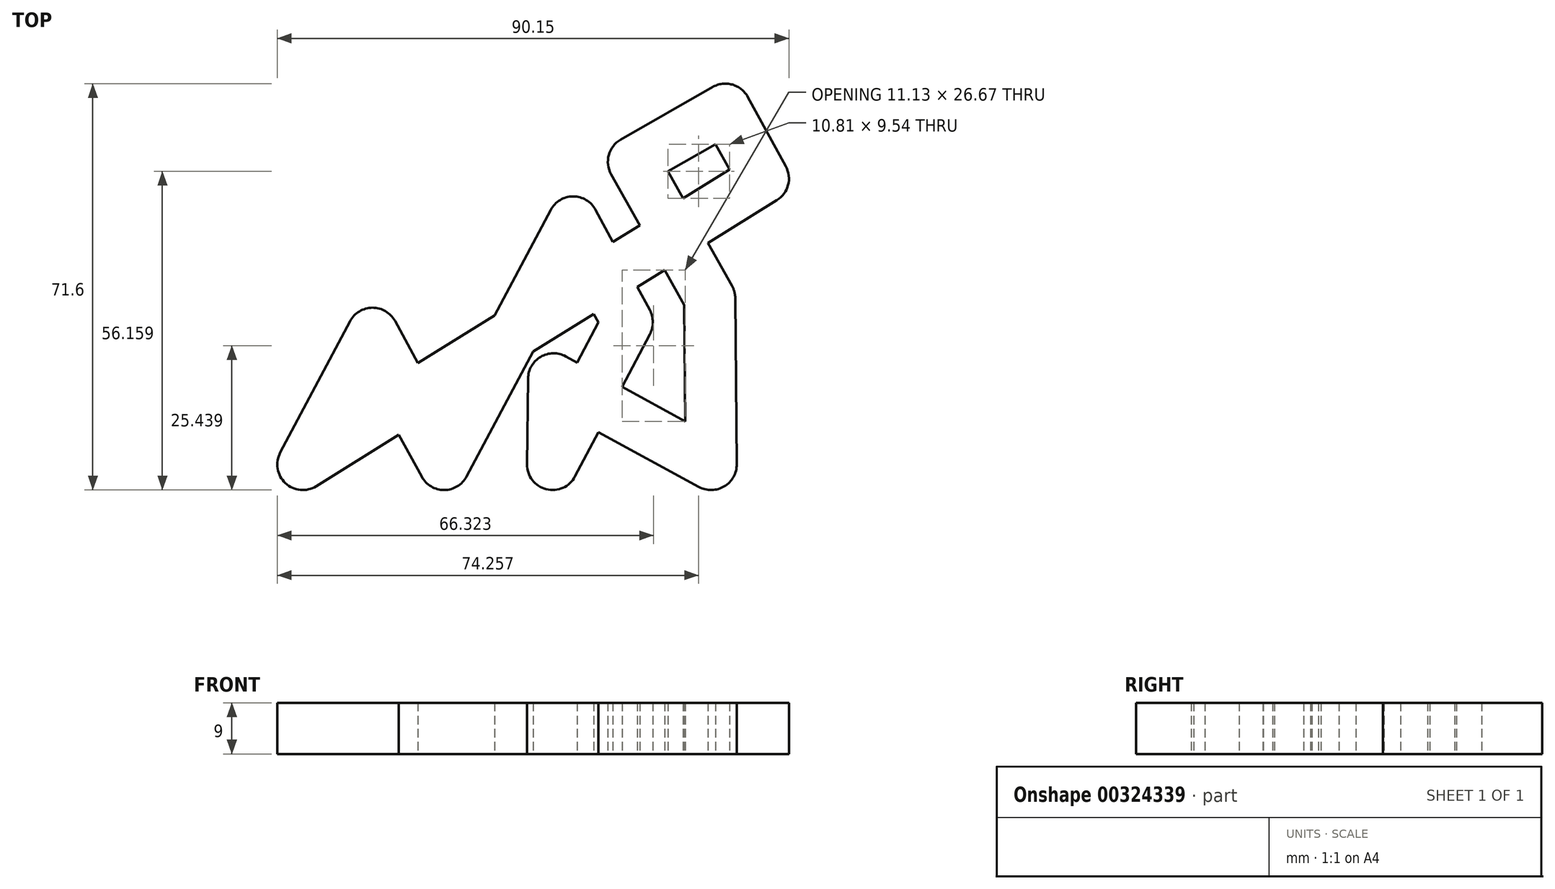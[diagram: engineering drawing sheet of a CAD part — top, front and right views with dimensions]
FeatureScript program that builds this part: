
annotation { "Feature Type Name" : "Feature", "Feature Type Description" : "" }
export const myFeature = defineFeature(function(context is Context, id is Id, definition is map)
    precondition{}
    {
        {
            var Q0;
            Q0=qCreatedBy(makeId("Top.planeOp"),FACE);
            var sketch = newSketch(context, id + "F0", { "sketchPlane" : qUnion([Q0])});
            skCircle(sketch, "E0", {"center": v(-54.94, 12.42) * mm, "radius": 4.5 * mm});
            skCircle(sketch, "E1", {"center": v(-67.23, -10.7) * mm, "radius": 4.5 * mm});
            skCircle(sketch, "E2", {"center": v(-42.34, -10.7) * mm, "radius": 4.5 * mm});
            skCircle(sketch, "E3", {"center": v(-23.23, -10.7) * mm, "radius": 4.5 * mm});
            skCircle(sketch, "E4", {"center": v(4.72, -10.7) * mm, "radius": 4.5 * mm});
            skCircle(sketch, "E5", {"center": v(-19.6, 32.03) * mm, "radius": 4.5 * mm});
            skCircle(sketch, "E6", {"center": v(13.92, 39.66) * mm, "radius": 4.5 * mm});
            skCircle(sketch, "E7", {"center": v(7.22, 51.9) * mm, "radius": 4.5 * mm});
            skCircle(sketch, "E8", {"center": v(-8.98, 42.62) * mm, "radius": 4.5 * mm});
            skCircle(sketch, "E9", {"center": v(4.47, 18.56) * mm, "radius": 4.5 * mm});
            skCircle(sketch, "E10", {"center": v(-10.06, 14.34) * mm, "radius": 4.5 * mm});
            skLineSegment(sketch, "E11", {"start": v(-58.92, 14.53) * mm, "end": v(-71.2, -8.6) * mm});
            skLineSegment(sketch, "E12", {"start": v(-63.26, -12.82) * mm, "end": v(-50.97, 10.3) * mm});
            skLineSegment(sketch, "E13", {"start": v(-51, 14.57) * mm, "end": v(-38.4, -8.56) * mm});
            skLineSegment(sketch, "E14", {"start": v(-58.9, 10.26) * mm, "end": v(-46.3, -12.86) * mm});
            skLineSegment(sketch, "E15", {"start": v(-69.6, -6.88) * mm, "end": v(11.55, 43.48) * mm});
            skCircle(sketch, "E16", {"center": v(-23.04, 4.38) * mm, "radius": 4.5 * mm});
            skLineSegment(sketch, "E17", {"start": v(-64.86, -14.53) * mm, "end": v(16.3, 35.84) * mm});
            skLineSegment(sketch, "E18", {"start": v(-38.37, -12.82) * mm, "end": v(-15.62, 29.91) * mm});
            skLineSegment(sketch, "E19", {"start": v(-46.32, -8.6) * mm, "end": v(-23.56, 34.14) * mm});
            skLineSegment(sketch, "E20", {"start": v(-23.55, 29.9) * mm, "end": v(-14.02, 12.2) * mm});
            skLineSegment(sketch, "E21", {"start": v(-15.63, 34.16) * mm, "end": v(-6.1, 16.47) * mm});
            skLineSegment(sketch, "E22", {"start": v(-6.08, 12.24) * mm, "end": v(-19.25, -12.8) * mm});
            skLineSegment(sketch, "E23", {"start": v(-14.04, 16.43) * mm, "end": v(-27.22, -8.61) * mm});
            skLineSegment(sketch, "E24", {"start": v(-27.73, -10.65) * mm, "end": v(-27.54, 4.44) * mm});
            skLineSegment(sketch, "E25", {"start": v(-18.73, -10.77) * mm, "end": v(-18.54, 4.32) * mm});
            skLineSegment(sketch, "E26", {"start": v(-25.19, 0.43) * mm, "end": v(2.57, -14.66) * mm});
            skLineSegment(sketch, "E27", {"start": v(-20.9, 8.33) * mm, "end": v(6.87, -6.75) * mm});
            skLineSegment(sketch, "E28", {"start": v(0.22, -10.75) * mm, "end": v(-0.03, 18.52) * mm});
            skLineSegment(sketch, "E29", {"start": v(9.22, -10.67) * mm, "end": v(8.97, 18.6) * mm});
            skLineSegment(sketch, "E30", {"start": v(8.4, 20.76) * mm, "end": v(-5.05, 44.81) * mm});
            skLineSegment(sketch, "E31", {"start": v(0.54, 16.37) * mm, "end": v(-12.9, 40.42) * mm});
            skLineSegment(sketch, "E32", {"start": v(-6.74, 38.71) * mm, "end": v(9.46, 48) * mm});
            skLineSegment(sketch, "E33", {"start": v(-11.21, 46.52) * mm, "end": v(4.99, 55.8) * mm});
            skLineSegment(sketch, "E34", {"start": v(3.28, 49.74) * mm, "end": v(9.97, 37.5) * mm});
            skLineSegment(sketch, "E35", {"start": v(11.16, 54.06) * mm, "end": v(17.87, 41.82) * mm});
            skSolve(sketch);
        }
        {
            var Q0;
            {var subQ0=sQuery(id+"F0.wireOp",EDGE,"E1");var subQ1=makeQuery(id+"F0.imprint","INTERSECT",VERTEX,{"derivedFrom":[subQ0,sQuery(id+"F0.wireOp",EDGE,"E11")]});Q0=makeQuery(id+"F0.imprint","IMPRINT",FACE,{"disambiguationData":[TD([[makeQuery(id+"F0.imprint","IMPRINT",EDGE,{"disambiguationData":[TD([[subQ1,1.0]])],"derivedFrom":subQ0}),1.0]])]});}
            var Q1;
            {var subQ0=sQuery(id+"F0.wireOp",EDGE,"E12");var subQ1=sQuery(id+"F0.wireOp",EDGE,"E1");var subQ2=makeQuery(id+"F0.imprint","INTERSECT",VERTEX,{"derivedFrom":[subQ1,subQ0]});Q1=makeQuery(id+"F0.imprint","IMPRINT",FACE,{"disambiguationData":[TD([[makeQuery(id+"F0.imprint","IMPRINT",EDGE,{"disambiguationData":[TD([[subQ2,-1.0]])],"derivedFrom":subQ1}),-1.0]])]});}
            var Q2;
            {var subQ0=sQuery(id+"F0.wireOp",EDGE,"E11");Q2=makeQuery(id+"F0.imprint","IMPRINT",FACE,{"disambiguationData":[TD([[makeQuery(id+"F0.imprint","IMPRINT",EDGE,{"derivedFrom":subQ0}),1.0]])]});}
            var Q3;
            {var subQ0=sQuery(id+"F0.wireOp",EDGE,"E12");var subQ1=sQuery(id+"F0.wireOp",EDGE,"E0");var subQ2=makeQuery(id+"F0.imprint","INTERSECT",VERTEX,{"derivedFrom":[subQ1,subQ0]});Q3=makeQuery(id+"F0.imprint","IMPRINT",FACE,{"disambiguationData":[TD([[makeQuery(id+"F0.imprint","IMPRINT",EDGE,{"disambiguationData":[TD([[subQ2,1.0]])],"derivedFrom":subQ1}),-1.0]])]});}
            var Q4;
            {var subQ0=sQuery(id+"F0.wireOp",EDGE,"E0");var subQ1=makeQuery(id+"F0.imprint","INTERSECT",VERTEX,{"derivedFrom":[subQ0,sQuery(id+"F0.wireOp",EDGE,"E11")]});Q4=makeQuery(id+"F0.imprint","IMPRINT",FACE,{"disambiguationData":[TD([[makeQuery(id+"F0.imprint","IMPRINT",EDGE,{"disambiguationData":[TD([[subQ1,1.0]])],"derivedFrom":subQ0}),1.0]])]});}
            var Q5;
            {var subQ1=sQuery(id+"F0.wireOp",EDGE,"E0");var subQ5=sQuery(id+"F0.wireOp",EDGE,"E12");var subQ6=makeQuery(id+"F0.imprint","INTERSECT",VERTEX,{"derivedFrom":[subQ1,subQ5]});Q5=makeQuery(id+"F0.imprint","IMPRINT",FACE,{"disambiguationData":[TD([[makeQuery(id+"F0.imprint","IMPRINT",EDGE,{"disambiguationData":[TD([[subQ6,-1.0]])],"derivedFrom":subQ1}),-1.0]])]});}
            var Q6;
            {var subQ0=sQuery(id+"F0.wireOp",EDGE,"E15");var subQ1=sQuery(id+"F0.wireOp",EDGE,"E13");var subQ2=makeQuery(id+"F0.imprint","INTERSECT",VERTEX,{"derivedFrom":[subQ1,subQ0]});Q6=makeQuery(id+"F0.imprint","IMPRINT",FACE,{"disambiguationData":[TD([[makeQuery(id+"F0.imprint","IMPRINT",EDGE,{"disambiguationData":[TD([[subQ2,-1.0]])],"derivedFrom":subQ1}),-1.0]])]});}
            var Q7;
            {var subQ0=sQuery(id+"F0.wireOp",EDGE,"E15");var subQ1=sQuery(id+"F0.wireOp",EDGE,"E12");var subQ2=makeQuery(id+"F0.imprint","INTERSECT",VERTEX,{"derivedFrom":[subQ1,subQ0]});Q7=makeQuery(id+"F0.imprint","IMPRINT",FACE,{"disambiguationData":[TD([[makeQuery(id+"F0.imprint","IMPRINT",EDGE,{"disambiguationData":[TD([[subQ2,-1.0]])],"derivedFrom":subQ1}),-1.0]])]});}
            var Q8;
            {var subQ1=sQuery(id+"F0.wireOp",EDGE,"E12");var subQ7=sQuery(id+"F0.wireOp",EDGE,"E1");var subQ8=makeQuery(id+"F0.imprint","INTERSECT",VERTEX,{"derivedFrom":[subQ7,subQ1]});Q8=makeQuery(id+"F0.imprint","IMPRINT",FACE,{"disambiguationData":[TD([[makeQuery(id+"F0.imprint","IMPRINT",EDGE,{"disambiguationData":[TD([[subQ8,1.0]])],"derivedFrom":subQ7}),-1.0]])]});}
            var Q9;
            {var subQ0=sQuery(id+"F0.wireOp",EDGE,"E15");var subQ1=sQuery(id+"F0.wireOp",EDGE,"E13");var subQ2=makeQuery(id+"F0.imprint","INTERSECT",VERTEX,{"derivedFrom":[subQ1,subQ0]});Q9=makeQuery(id+"F0.imprint","IMPRINT",FACE,{"disambiguationData":[TD([[makeQuery(id+"F0.imprint","IMPRINT",EDGE,{"disambiguationData":[TD([[subQ2,-1.0]])],"derivedFrom":subQ1}),1.0]])]});}
            var Q10;
            {var subQ1=sQuery(id+"F0.wireOp",EDGE,"E14");var subQ5=sQuery(id+"F0.wireOp",EDGE,"E2");var subQ6=makeQuery(id+"F0.imprint","INTERSECT",VERTEX,{"derivedFrom":[subQ5,subQ1]});Q10=makeQuery(id+"F0.imprint","IMPRINT",FACE,{"disambiguationData":[TD([[makeQuery(id+"F0.imprint","IMPRINT",EDGE,{"disambiguationData":[TD([[subQ6,1.0]])],"derivedFrom":subQ5}),-1.0]])]});}
            var Q11;
            {var subQ0=sQuery(id+"F0.wireOp",EDGE,"E17");var subQ1=sQuery(id+"F0.wireOp",EDGE,"E13");var subQ2=makeQuery(id+"F0.imprint","INTERSECT",VERTEX,{"derivedFrom":[subQ1,subQ0]});Q11=makeQuery(id+"F0.imprint","IMPRINT",FACE,{"disambiguationData":[TD([[makeQuery(id+"F0.imprint","IMPRINT",EDGE,{"disambiguationData":[TD([[subQ2,-1.0]])],"derivedFrom":subQ1}),1.0]])]});}
            var Q12;
            {var subQ0=sQuery(id+"F0.wireOp",EDGE,"E13");var subQ1=sQuery(id+"F0.wireOp",EDGE,"E2");var subQ2=makeQuery(id+"F0.imprint","INTERSECT",VERTEX,{"derivedFrom":[subQ1,subQ0]});Q12=makeQuery(id+"F0.imprint","IMPRINT",FACE,{"disambiguationData":[TD([[makeQuery(id+"F0.imprint","IMPRINT",EDGE,{"disambiguationData":[TD([[subQ2,-1.0]])],"derivedFrom":subQ1}),-1.0]])]});}
            var Q13;
            {var subQ5=sQuery(id+"F0.wireOp",EDGE,"E2");var subQ7=sQuery(id+"F0.wireOp",EDGE,"E13");var subQ8=makeQuery(id+"F0.imprint","INTERSECT",VERTEX,{"derivedFrom":[subQ5,subQ7]});Q13=makeQuery(id+"F0.imprint","IMPRINT",FACE,{"disambiguationData":[TD([[makeQuery(id+"F0.imprint","IMPRINT",EDGE,{"disambiguationData":[TD([[subQ8,1.0]])],"derivedFrom":subQ5}),-1.0]])]});}
            var Q14;
            {var subQ5=sQuery(id+"F0.wireOp",EDGE,"E19");var subQ6=sQuery(id+"F0.wireOp",EDGE,"E15");var subQ7=makeQuery(id+"F0.imprint","INTERSECT",VERTEX,{"derivedFrom":[subQ6,subQ5]});Q14=makeQuery(id+"F0.imprint","IMPRINT",FACE,{"disambiguationData":[TD([[makeQuery(id+"F0.imprint","IMPRINT",EDGE,{"disambiguationData":[TD([[subQ7,-1.0]])],"derivedFrom":subQ6}),-1.0]])]});}
            var Q15;
            {var subQ0=sQuery(id+"F0.wireOp",EDGE,"E2");var subQ1=makeQuery(id+"F0.imprint","INTERSECT",VERTEX,{"derivedFrom":[subQ0,sQuery(id+"F0.wireOp",EDGE,"E13")]});Q15=makeQuery(id+"F0.imprint","IMPRINT",FACE,{"disambiguationData":[TD([[makeQuery(id+"F0.imprint","IMPRINT",EDGE,{"disambiguationData":[TD([[subQ1,-1.0]])],"derivedFrom":subQ0}),1.0]])]});}
            var Q16;
            {var subQ0=sQuery(id+"F0.wireOp",EDGE,"E3");var subQ1=makeQuery(id+"F0.imprint","INTERSECT",VERTEX,{"derivedFrom":[subQ0,sQuery(id+"F0.wireOp",EDGE,"E23")]});Q16=makeQuery(id+"F0.imprint","IMPRINT",FACE,{"disambiguationData":[TD([[makeQuery(id+"F0.imprint","IMPRINT",EDGE,{"disambiguationData":[TD([[subQ1,-1.0]])],"derivedFrom":subQ0}),1.0]])]});}
            var Q17;
            {var subQ0=sQuery(id+"F0.wireOp",EDGE,"E23");var subQ1=sQuery(id+"F0.wireOp",EDGE,"E3");var subQ2=makeQuery(id+"F0.imprint","INTERSECT",VERTEX,{"derivedFrom":[subQ1,subQ0]});Q17=makeQuery(id+"F0.imprint","IMPRINT",FACE,{"disambiguationData":[TD([[makeQuery(id+"F0.imprint","IMPRINT",EDGE,{"disambiguationData":[TD([[subQ2,1.0]])],"derivedFrom":subQ1}),-1.0]])]});}
            var Q18;
            {var subQ0=sQuery(id+"F0.wireOp",EDGE,"E24");Q18=makeQuery(id+"F0.imprint","IMPRINT",FACE,{"disambiguationData":[TD([[makeQuery(id+"F0.imprint","IMPRINT",EDGE,{"derivedFrom":subQ0}),-1.0]])]});}
            var Q19;
            {var subQ0=sQuery(id+"F0.wireOp",EDGE,"E26");var subQ1=sQuery(id+"F0.wireOp",EDGE,"E16");var subQ2=makeQuery(id+"F0.imprint","INTERSECT",VERTEX,{"derivedFrom":[subQ1,subQ0]});Q19=makeQuery(id+"F0.imprint","IMPRINT",FACE,{"disambiguationData":[TD([[makeQuery(id+"F0.imprint","IMPRINT",EDGE,{"disambiguationData":[TD([[subQ2,-1.0]])],"derivedFrom":subQ1}),-1.0]])]});}
            var Q20;
            {var subQ0=sQuery(id+"F0.wireOp",EDGE,"E16");var subQ5=makeQuery(id+"F0.imprint","INTERSECT",VERTEX,{"derivedFrom":[subQ0,sQuery(id+"F0.wireOp",EDGE,"E27")]});Q20=makeQuery(id+"F0.imprint","IMPRINT",FACE,{"disambiguationData":[TD([[makeQuery(id+"F0.imprint","IMPRINT",EDGE,{"disambiguationData":[TD([[subQ5,1.0]])],"derivedFrom":subQ0}),1.0]])]});}
            var Q21;
            {var subQ0=sQuery(id+"F0.wireOp",EDGE,"E16");var subQ1=makeQuery(id+"F0.imprint","INTERSECT",VERTEX,{"derivedFrom":[subQ0,sQuery(id+"F0.wireOp",EDGE,"E25")]});Q21=makeQuery(id+"F0.imprint","IMPRINT",FACE,{"disambiguationData":[TD([[makeQuery(id+"F0.imprint","IMPRINT",EDGE,{"disambiguationData":[TD([[subQ1,1.0]])],"derivedFrom":subQ0}),1.0]])]});}
            var Q22;
            {var subQ0=sQuery(id+"F0.wireOp",EDGE,"E25");var subQ1=sQuery(id+"F0.wireOp",EDGE,"E16");var subQ2=makeQuery(id+"F0.imprint","INTERSECT",VERTEX,{"derivedFrom":[subQ1,subQ0]});Q22=makeQuery(id+"F0.imprint","IMPRINT",FACE,{"disambiguationData":[TD([[makeQuery(id+"F0.imprint","IMPRINT",EDGE,{"disambiguationData":[TD([[subQ2,1.0]])],"derivedFrom":subQ1}),-1.0]])]});}
            var Q23;
            {var subQ0=sQuery(id+"F0.wireOp",EDGE,"E25");var subQ1=sQuery(id+"F0.wireOp",EDGE,"E16");var subQ2=makeQuery(id+"F0.imprint","INTERSECT",VERTEX,{"derivedFrom":[subQ1,subQ0]});Q23=makeQuery(id+"F0.imprint","IMPRINT",FACE,{"disambiguationData":[TD([[makeQuery(id+"F0.imprint","IMPRINT",EDGE,{"disambiguationData":[TD([[subQ2,-1.0]])],"derivedFrom":subQ1}),-1.0]])]});}
            var Q24;
            {var subQ5=sQuery(id+"F0.wireOp",EDGE,"E26");var subQ7=sQuery(id+"F0.wireOp",EDGE,"E4");var subQ8=makeQuery(id+"F0.imprint","INTERSECT",VERTEX,{"derivedFrom":[subQ7,subQ5]});Q24=makeQuery(id+"F0.imprint","IMPRINT",FACE,{"disambiguationData":[TD([[makeQuery(id+"F0.imprint","IMPRINT",EDGE,{"disambiguationData":[TD([[subQ8,1.0]])],"derivedFrom":subQ7}),-1.0]])]});}
            var Q25;
            {var subQ0=sQuery(id+"F0.wireOp",EDGE,"E27");var subQ1=sQuery(id+"F0.wireOp",EDGE,"E4");var subQ2=makeQuery(id+"F0.imprint","INTERSECT",VERTEX,{"derivedFrom":[subQ1,subQ0]});Q25=makeQuery(id+"F0.imprint","IMPRINT",FACE,{"disambiguationData":[TD([[makeQuery(id+"F0.imprint","IMPRINT",EDGE,{"disambiguationData":[TD([[subQ2,-1.0]])],"derivedFrom":subQ1}),-1.0]])]});}
            var Q26;
            {var subQ0=sQuery(id+"F0.wireOp",EDGE,"E27");var subQ1=sQuery(id+"F0.wireOp",EDGE,"E16");var subQ2=makeQuery(id+"F0.imprint","INTERSECT",VERTEX,{"derivedFrom":[subQ1,subQ0]});Q26=makeQuery(id+"F0.imprint","IMPRINT",FACE,{"disambiguationData":[TD([[makeQuery(id+"F0.imprint","IMPRINT",EDGE,{"disambiguationData":[TD([[subQ2,1.0]])],"derivedFrom":subQ1}),-1.0]])]});}
            var Q27;
            {var subQ1=sQuery(id+"F0.wireOp",EDGE,"E20");var subQ6=sQuery(id+"F0.wireOp",EDGE,"E10");var subQ9=makeQuery(id+"F0.imprint","INTERSECT",VERTEX,{"derivedFrom":[subQ6,subQ1]});Q27=makeQuery(id+"F0.imprint","IMPRINT",FACE,{"disambiguationData":[TD([[makeQuery(id+"F0.imprint","IMPRINT",EDGE,{"disambiguationData":[TD([[subQ9,-1.0]])],"derivedFrom":subQ6}),-1.0]])]});}
            var Q28;
            {var subQ0=sQuery(id+"F0.wireOp",EDGE,"E20");var subQ1=sQuery(id+"F0.wireOp",EDGE,"E10");var subQ2=makeQuery(id+"F0.imprint","INTERSECT",VERTEX,{"derivedFrom":[subQ1,subQ0]});Q28=makeQuery(id+"F0.imprint","IMPRINT",FACE,{"disambiguationData":[TD([[makeQuery(id+"F0.imprint","IMPRINT",EDGE,{"disambiguationData":[TD([[subQ2,1.0]])],"derivedFrom":subQ1}),-1.0]])]});}
            var Q29;
            {var subQ0=sQuery(id+"F0.wireOp",EDGE,"E23");var subQ1=sQuery(id+"F0.wireOp",EDGE,"E10");var subQ2=makeQuery(id+"F0.imprint","INTERSECT",VERTEX,{"derivedFrom":[subQ1,subQ0]});Q29=makeQuery(id+"F0.imprint","IMPRINT",FACE,{"disambiguationData":[TD([[makeQuery(id+"F0.imprint","IMPRINT",EDGE,{"disambiguationData":[TD([[subQ2,1.0]])],"derivedFrom":subQ1}),-1.0]])]});}
            var Q30;
            {var subQ0=sQuery(id+"F0.wireOp",EDGE,"E10");var subQ6=makeQuery(id+"F0.imprint","INTERSECT",VERTEX,{"derivedFrom":[subQ0,sQuery(id+"F0.wireOp",EDGE,"E21")]});Q30=makeQuery(id+"F0.imprint","IMPRINT",FACE,{"disambiguationData":[TD([[makeQuery(id+"F0.imprint","IMPRINT",EDGE,{"disambiguationData":[TD([[subQ6,-1.0]])],"derivedFrom":subQ0}),1.0]])]});}
            var Q31;
            {var subQ0=sQuery(id+"F0.wireOp",EDGE,"E20");var subQ1=sQuery(id+"F0.wireOp",EDGE,"E15");var subQ2=makeQuery(id+"F0.imprint","INTERSECT",VERTEX,{"derivedFrom":[subQ1,subQ0]});Q31=makeQuery(id+"F0.imprint","IMPRINT",FACE,{"disambiguationData":[TD([[makeQuery(id+"F0.imprint","IMPRINT",EDGE,{"disambiguationData":[TD([[subQ2,-1.0]])],"derivedFrom":subQ1}),-1.0]])]});}
            var Q32;
            {var subQ0=sQuery(id+"F0.wireOp",EDGE,"E18");var subQ1=sQuery(id+"F0.wireOp",EDGE,"E5");var subQ2=makeQuery(id+"F0.imprint","INTERSECT",VERTEX,{"derivedFrom":[subQ1,subQ0]});Q32=makeQuery(id+"F0.imprint","IMPRINT",FACE,{"disambiguationData":[TD([[makeQuery(id+"F0.imprint","IMPRINT",EDGE,{"disambiguationData":[TD([[subQ2,1.0]])],"derivedFrom":subQ1}),-1.0]])]});}
            var Q33;
            {var subQ0=sQuery(id+"F0.wireOp",EDGE,"E19");var subQ1=sQuery(id+"F0.wireOp",EDGE,"E5");var subQ2=makeQuery(id+"F0.imprint","INTERSECT",VERTEX,{"derivedFrom":[subQ1,subQ0]});Q33=makeQuery(id+"F0.imprint","IMPRINT",FACE,{"disambiguationData":[TD([[makeQuery(id+"F0.imprint","IMPRINT",EDGE,{"disambiguationData":[TD([[subQ2,-1.0]])],"derivedFrom":subQ1}),-1.0]])]});}
            var Q34;
            {var subQ0=sQuery(id+"F0.wireOp",EDGE,"E5");var subQ1=makeQuery(id+"F0.imprint","INTERSECT",VERTEX,{"derivedFrom":[subQ0,sQuery(id+"F0.wireOp",EDGE,"E19")]});Q34=makeQuery(id+"F0.imprint","IMPRINT",FACE,{"disambiguationData":[TD([[makeQuery(id+"F0.imprint","IMPRINT",EDGE,{"disambiguationData":[TD([[subQ1,1.0]])],"derivedFrom":subQ0}),1.0]])]});}
            var Q35;
            {var subQ0=sQuery(id+"F0.wireOp",EDGE,"E18");var subQ1=sQuery(id+"F0.wireOp",EDGE,"E5");var subQ2=makeQuery(id+"F0.imprint","INTERSECT",VERTEX,{"derivedFrom":[subQ1,subQ0]});Q35=makeQuery(id+"F0.imprint","IMPRINT",FACE,{"disambiguationData":[TD([[makeQuery(id+"F0.imprint","IMPRINT",EDGE,{"disambiguationData":[TD([[subQ2,-1.0]])],"derivedFrom":subQ1}),-1.0]])]});}
            var Q36;
            {var subQ0=sQuery(id+"F0.wireOp",EDGE,"E17");var subQ1=sQuery(id+"F0.wireOp",EDGE,"E10");var subQ2=makeQuery(id+"F0.imprint","INTERSECT",VERTEX,{"disambiguationData":[OD(0.0)],"derivedFrom":[subQ1,subQ0]});Q36=makeQuery(id+"F0.imprint","IMPRINT",FACE,{"disambiguationData":[TD([[makeQuery(id+"F0.imprint","IMPRINT",EDGE,{"disambiguationData":[TD([[subQ2,-1.0]])],"derivedFrom":subQ1}),-1.0]])]});}
            var Q37;
            {var subQ0=sQuery(id+"F0.wireOp",EDGE,"E21");var subQ1=sQuery(id+"F0.wireOp",EDGE,"E15");var subQ2=makeQuery(id+"F0.imprint","INTERSECT",VERTEX,{"derivedFrom":[subQ1,subQ0]});Q37=makeQuery(id+"F0.imprint","IMPRINT",FACE,{"disambiguationData":[TD([[makeQuery(id+"F0.imprint","IMPRINT",EDGE,{"disambiguationData":[TD([[subQ2,-1.0]])],"derivedFrom":subQ1}),-1.0]])]});}
            var Q38;
            {var subQ5=sQuery(id+"F0.wireOp",EDGE,"E31");var subQ6=sQuery(id+"F0.wireOp",EDGE,"E8");var subQ7=makeQuery(id+"F0.imprint","INTERSECT",VERTEX,{"derivedFrom":[subQ6,subQ5]});Q38=makeQuery(id+"F0.imprint","IMPRINT",FACE,{"disambiguationData":[TD([[makeQuery(id+"F0.imprint","IMPRINT",EDGE,{"disambiguationData":[TD([[subQ7,-1.0]])],"derivedFrom":subQ6}),-1.0]])]});}
            var Q39;
            {var subQ0=sQuery(id+"F0.wireOp",EDGE,"E8");var subQ1=makeQuery(id+"F0.imprint","INTERSECT",VERTEX,{"derivedFrom":[subQ0,sQuery(id+"F0.wireOp",EDGE,"E30")]});Q39=makeQuery(id+"F0.imprint","IMPRINT",FACE,{"disambiguationData":[TD([[makeQuery(id+"F0.imprint","IMPRINT",EDGE,{"disambiguationData":[TD([[subQ1,-1.0]])],"derivedFrom":subQ0}),1.0]])]});}
            var Q40;
            {var subQ0=sQuery(id+"F0.wireOp",EDGE,"E30");var subQ1=sQuery(id+"F0.wireOp",EDGE,"E8");var subQ2=makeQuery(id+"F0.imprint","INTERSECT",VERTEX,{"derivedFrom":[subQ1,subQ0]});Q40=makeQuery(id+"F0.imprint","IMPRINT",FACE,{"disambiguationData":[TD([[makeQuery(id+"F0.imprint","IMPRINT",EDGE,{"disambiguationData":[TD([[subQ2,1.0]])],"derivedFrom":subQ1}),-1.0]])]});}
            var Q41;
            {var subQ7=sQuery(id+"F0.wireOp",EDGE,"E33");Q41=makeQuery(id+"F0.imprint","IMPRINT",FACE,{"disambiguationData":[TD([[makeQuery(id+"F0.imprint","IMPRINT",EDGE,{"derivedFrom":subQ7}),-1.0]])]});}
            var Q42;
            {var subQ0=sQuery(id+"F0.wireOp",EDGE,"E32");var subQ1=sQuery(id+"F0.wireOp",EDGE,"E7");var subQ2=makeQuery(id+"F0.imprint","INTERSECT",VERTEX,{"derivedFrom":[subQ1,subQ0]});Q42=makeQuery(id+"F0.imprint","IMPRINT",FACE,{"disambiguationData":[TD([[makeQuery(id+"F0.imprint","IMPRINT",EDGE,{"disambiguationData":[TD([[subQ2,1.0]])],"derivedFrom":subQ1}),-1.0]])]});}
            var Q43;
            {var subQ0=sQuery(id+"F0.wireOp",EDGE,"E7");var subQ1=makeQuery(id+"F0.imprint","INTERSECT",VERTEX,{"derivedFrom":[subQ0,sQuery(id+"F0.wireOp",EDGE,"E33")]});Q43=makeQuery(id+"F0.imprint","IMPRINT",FACE,{"disambiguationData":[TD([[makeQuery(id+"F0.imprint","IMPRINT",EDGE,{"disambiguationData":[TD([[subQ1,1.0]])],"derivedFrom":subQ0}),1.0]])]});}
            var Q44;
            {var subQ9=sQuery(id+"F0.wireOp",EDGE,"E35");Q44=makeQuery(id+"F0.imprint","IMPRINT",FACE,{"disambiguationData":[TD([[makeQuery(id+"F0.imprint","IMPRINT",EDGE,{"derivedFrom":subQ9}),-1.0]])]});}
            var Q45;
            {var subQ0=sQuery(id+"F0.wireOp",EDGE,"E15");var subQ1=sQuery(id+"F0.wireOp",EDGE,"E6");var subQ2=makeQuery(id+"F0.imprint","INTERSECT",VERTEX,{"derivedFrom":[subQ1,subQ0]});Q45=makeQuery(id+"F0.imprint","IMPRINT",FACE,{"disambiguationData":[TD([[makeQuery(id+"F0.imprint","IMPRINT",EDGE,{"disambiguationData":[TD([[subQ2,-1.0]])],"derivedFrom":subQ1}),-1.0]])]});}
            var Q46;
            {var subQ0=sQuery(id+"F0.wireOp",EDGE,"E6");var subQ1=makeQuery(id+"F0.imprint","INTERSECT",VERTEX,{"derivedFrom":[subQ0,sQuery(id+"F0.wireOp",EDGE,"E15")]});Q46=makeQuery(id+"F0.imprint","IMPRINT",FACE,{"disambiguationData":[TD([[makeQuery(id+"F0.imprint","IMPRINT",EDGE,{"disambiguationData":[TD([[subQ1,1.0]])],"derivedFrom":subQ0}),1.0]])]});}
            var Q47;
            {var subQ0=sQuery(id+"F0.wireOp",EDGE,"E17");var subQ1=sQuery(id+"F0.wireOp",EDGE,"E6");var subQ2=makeQuery(id+"F0.imprint","INTERSECT",VERTEX,{"derivedFrom":[subQ1,subQ0]});Q47=makeQuery(id+"F0.imprint","IMPRINT",FACE,{"disambiguationData":[TD([[makeQuery(id+"F0.imprint","IMPRINT",EDGE,{"disambiguationData":[TD([[subQ2,1.0]])],"derivedFrom":subQ1}),-1.0]])]});}
            var Q48;
            {var subQ0=sQuery(id+"F0.wireOp",EDGE,"E17");var subQ1=sQuery(id+"F0.wireOp",EDGE,"E10");var subQ2=makeQuery(id+"F0.imprint","INTERSECT",VERTEX,{"disambiguationData":[OD(0.0)],"derivedFrom":[subQ1,subQ0]});Q48=makeQuery(id+"F0.imprint","IMPRINT",FACE,{"disambiguationData":[TD([[makeQuery(id+"F0.imprint","IMPRINT",EDGE,{"disambiguationData":[TD([[subQ2,-1.0]])],"derivedFrom":subQ1}),1.0]])]});}
            var Q49;
            {var subQ0=sQuery(id+"F0.wireOp",EDGE,"E31");var subQ1=sQuery(id+"F0.wireOp",EDGE,"E15");var subQ2=makeQuery(id+"F0.imprint","INTERSECT",VERTEX,{"derivedFrom":[subQ1,subQ0]});Q49=makeQuery(id+"F0.imprint","IMPRINT",FACE,{"disambiguationData":[TD([[makeQuery(id+"F0.imprint","IMPRINT",EDGE,{"disambiguationData":[TD([[subQ2,-1.0]])],"derivedFrom":subQ1}),-1.0]])]});}
            var Q50;
            {var subQ1=sQuery(id+"F0.wireOp",EDGE,"E9");var subQ5=sQuery(id+"F0.wireOp",EDGE,"E28");var subQ6=makeQuery(id+"F0.imprint","INTERSECT",VERTEX,{"derivedFrom":[subQ1,subQ5]});Q50=makeQuery(id+"F0.imprint","IMPRINT",FACE,{"disambiguationData":[TD([[makeQuery(id+"F0.imprint","IMPRINT",EDGE,{"disambiguationData":[TD([[subQ6,1.0]])],"derivedFrom":subQ1}),-1.0]])]});}
            var Q51;
            {var subQ0=sQuery(id+"F0.wireOp",EDGE,"E9");var subQ1=makeQuery(id+"F0.imprint","INTERSECT",VERTEX,{"derivedFrom":[subQ0,sQuery(id+"F0.wireOp",EDGE,"E29")]});Q51=makeQuery(id+"F0.imprint","IMPRINT",FACE,{"disambiguationData":[TD([[makeQuery(id+"F0.imprint","IMPRINT",EDGE,{"disambiguationData":[TD([[subQ1,-1.0]])],"derivedFrom":subQ0}),1.0]])]});}
            var Q52;
            {var subQ7=sQuery(id+"F0.wireOp",EDGE,"E29");Q52=makeQuery(id+"F0.imprint","IMPRINT",FACE,{"disambiguationData":[TD([[makeQuery(id+"F0.imprint","IMPRINT",EDGE,{"derivedFrom":subQ7}),1.0]])]});}
            var Q53;
            {var subQ0=sQuery(id+"F0.wireOp",EDGE,"E4");var subQ1=makeQuery(id+"F0.imprint","INTERSECT",VERTEX,{"derivedFrom":[subQ0,sQuery(id+"F0.wireOp",EDGE,"E27")]});Q53=makeQuery(id+"F0.imprint","IMPRINT",FACE,{"disambiguationData":[TD([[makeQuery(id+"F0.imprint","IMPRINT",EDGE,{"disambiguationData":[TD([[subQ1,1.0]])],"derivedFrom":subQ0}),1.0]])]});}
            var Q54;
            {var subQ0=sQuery(id+"F0.wireOp",EDGE,"E28");var subQ1=sQuery(id+"F0.wireOp",EDGE,"E9");var subQ2=makeQuery(id+"F0.imprint","INTERSECT",VERTEX,{"derivedFrom":[subQ1,subQ0]});Q54=makeQuery(id+"F0.imprint","IMPRINT",FACE,{"disambiguationData":[TD([[makeQuery(id+"F0.imprint","IMPRINT",EDGE,{"disambiguationData":[TD([[subQ2,-1.0]])],"derivedFrom":subQ1}),-1.0]])]});}
            var Q55;
            {var subQ0=sQuery(id+"F0.wireOp",EDGE,"E21");var subQ1=sQuery(id+"F0.wireOp",EDGE,"E10");var subQ2=makeQuery(id+"F0.imprint","INTERSECT",VERTEX,{"derivedFrom":[subQ1,subQ0]});Q55=makeQuery(id+"F0.imprint","IMPRINT",FACE,{"disambiguationData":[TD([[makeQuery(id+"F0.imprint","IMPRINT",EDGE,{"disambiguationData":[TD([[subQ2,-1.0]])],"derivedFrom":subQ1}),-1.0]])]});}
            var Q56;
            {var subQ0=sQuery(id+"F0.wireOp",EDGE,"E18");var subQ1=sQuery(id+"F0.wireOp",EDGE,"E17");var subQ2=makeQuery(id+"F0.imprint","INTERSECT",VERTEX,{"derivedFrom":[subQ1,subQ0]});Q56=makeQuery(id+"F0.imprint","IMPRINT",FACE,{"disambiguationData":[TD([[makeQuery(id+"F0.imprint","IMPRINT",EDGE,{"disambiguationData":[TD([[subQ2,-1.0]])],"derivedFrom":subQ1}),1.0]])]});}
            var Q57;
            {var subQ0=sQuery(id+"F0.wireOp",EDGE,"E22");var subQ1=sQuery(id+"F0.wireOp",EDGE,"E3");var subQ2=makeQuery(id+"F0.imprint","INTERSECT",VERTEX,{"derivedFrom":[subQ1,subQ0]});Q57=makeQuery(id+"F0.imprint","IMPRINT",FACE,{"disambiguationData":[TD([[makeQuery(id+"F0.imprint","IMPRINT",EDGE,{"disambiguationData":[TD([[subQ2,-1.0]])],"derivedFrom":subQ1}),-1.0]])]});}
            extrude(context, id + "F1", {"entities" : qUnion([Q0, Q1, Q2, Q3, Q4, Q5, Q6, Q7, Q8, Q9, Q10, Q11, Q12, Q13, Q14, Q15, Q16, Q17, Q18, Q19, Q20, Q21, Q22, Q23, Q24, Q25, Q26, Q27, Q28, Q29, Q30, Q31, Q32, Q33, Q34, Q35, Q36, Q37, Q38, Q39, Q40, Q41, Q42, Q43, Q44, Q45, Q46, Q47, Q48, Q49, Q50, Q51, Q52, Q53, Q54, Q55, Q56, Q57]), "depth" : 9 * mm});
        }
    });
